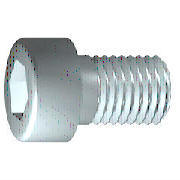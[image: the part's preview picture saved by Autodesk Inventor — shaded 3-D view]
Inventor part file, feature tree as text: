
AUTODESK INVENTOR PART (.ipt)
format: ipt  version: 2022 (Build 260153000, 153)  size: 192,000 bytes
history: native  units: mm (DEFAULTED — no unit token found)
features: sketch x2, other x1, extrude x1, plane x1, fillet x1
ambient origin geometry x7: Origin, YZ Plane, XY Plane, X Axis, Y Axis, Z Axis, Center Point
bodies: Solid1 (feature_tree)
feature tree (6):
  other  "Базовый элемент"
  extrude  "Паз"  Depth=14.75mm
  plane  "Work Plane1"
  fillet  "Fillet2"  Radius=0.306825mm
  sketch  "Эскиз1"
  sketch  "Эскиз2"
